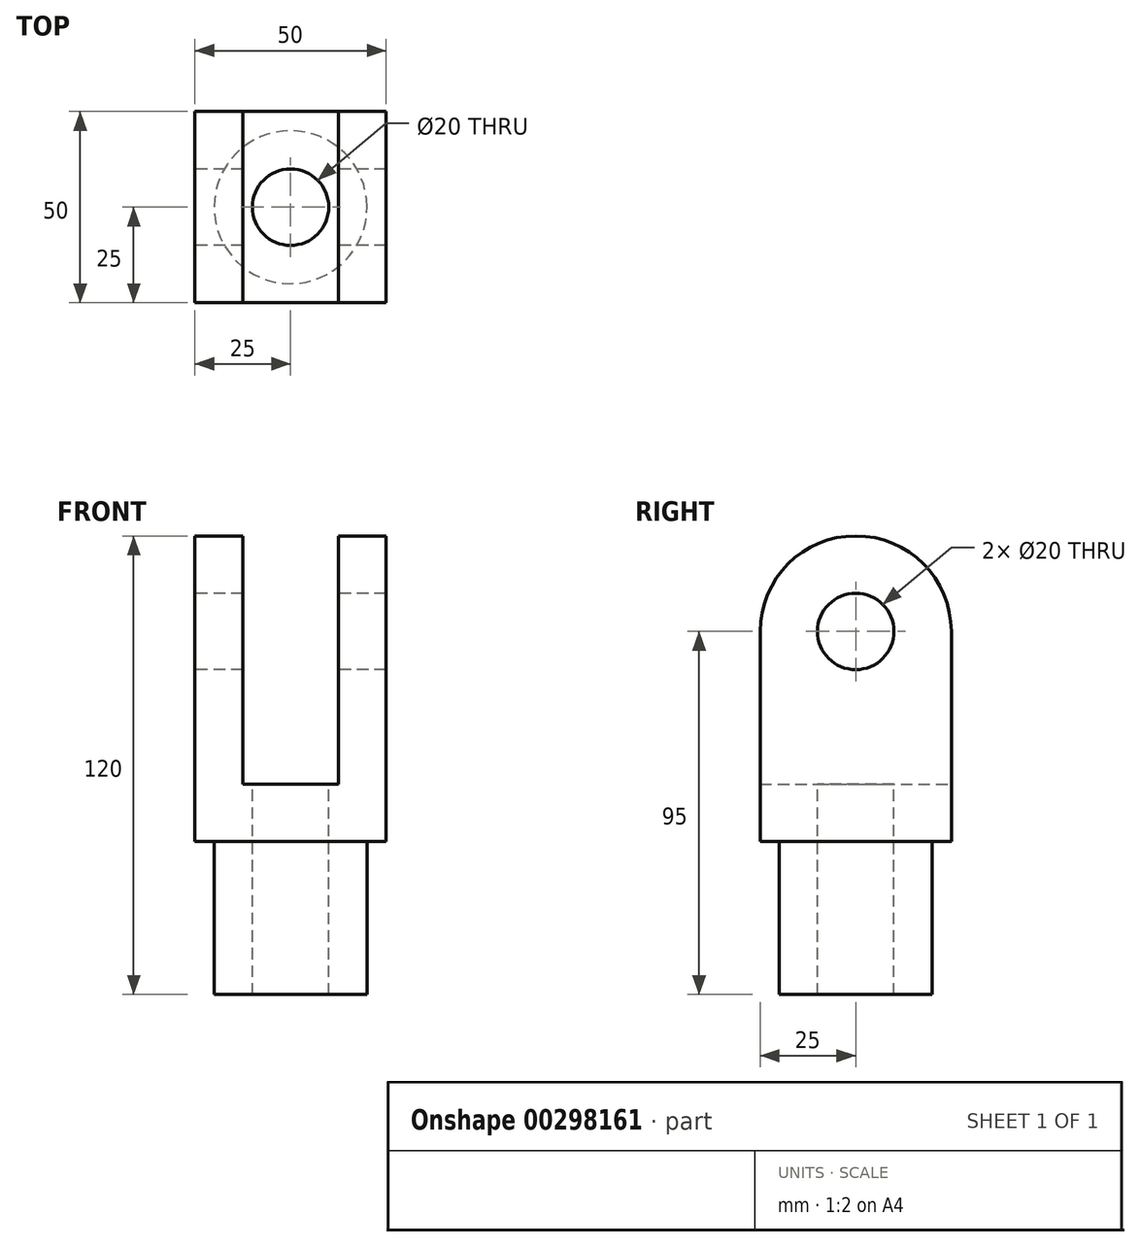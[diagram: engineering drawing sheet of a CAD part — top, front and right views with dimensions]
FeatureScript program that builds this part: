
annotation { "Feature Type Name" : "Feature", "Feature Type Description" : "" }
export const myFeature = defineFeature(function(context is Context, id is Id, definition is map)
    precondition{}
    {
        {
            var Q0;
            Q0=qCreatedBy(makeId("Front.planeOp"),FACE);
            var sketch = newSketch(context, id + "F0", { "sketchPlane" : qUnion([Q0])});
            skLineSegment(sketch, "E0.bottom", {"start": v(-25, 40) * mm, "end": v(25, 40) * mm});
            skLineSegment(sketch, "E0.top", {"start": v(-25, -40) * mm, "end": v(25, -40) * mm});
            skLineSegment(sketch, "E0.left", {"start": v(-25, 40) * mm, "end": v(-25, -40) * mm});
            skLineSegment(sketch, "E0.right", {"start": v(25, 40) * mm, "end": v(25, -40) * mm});
            skPoint(sketch, "E0.middle", {"position": v(0, 0) * mm});
            skLineSegment(sketch, "E1.bottom", {"start": v(12.5, 105) * mm, "end": v(-12.5, 105) * mm});
            skLineSegment(sketch, "E1.top", {"start": v(12.5, -25) * mm, "end": v(-12.5, -25) * mm});
            skLineSegment(sketch, "E1.left", {"start": v(12.5, 105) * mm, "end": v(12.5, -25) * mm});
            skLineSegment(sketch, "E1.right", {"start": v(-12.5, 105) * mm, "end": v(-12.5, -25) * mm});
            skPoint(sketch, "E1.middle", {"position": v(0, 40) * mm});
            skSolve(sketch);
        }
        {
            var Q0;
            Q0=makeQuery(id+"F0.imprint","IMPRINT",FACE,{"disambiguationData":[TD([[makeQuery(id+"F0.imprint","IMPRINT",EDGE,{"derivedFrom":sQuery(id+"F0.wireOp",EDGE,"E0.top")}),1.0]])]});
            extrude(context, id + "F1", {"entities" : qUnion([Q0]), "endBound" : BoundingType.SYMMETRIC, "depth" : 50 * mm});
        }
        {
            var Q0;
            Q0=makeQuery(id+"F1.opExtrude","SWEPT_FACE",FACE,{"disambiguationData":[OSD([sQuery(id+"F0.wireOp",EDGE,"E0.top")])]});
            var sketch = newSketch(context, id + "F2", { "sketchPlane" : qUnion([Q0])});
            skCircle(sketch, "E2", {"center": v(0, 0) * mm, "radius": 10 * mm});
            skCircle(sketch, "E3", {"center": v(0, 0) * mm, "radius": 20 * mm});
            skSolve(sketch);
        }
        {
            var Q0;
            Q0=makeQuery(id+"F2.imprint","IMPRINT",FACE,{"disambiguationData":[TD([[makeQuery(id+"F2.imprint","IMPRINT",EDGE,{"derivedFrom":sQuery(id+"F2.wireOp",EDGE,"E2")}),-1.0]])]});
            extrude(context, id + "F3", {"entities" : qUnion([Q0]), "operationType" : NewBodyOperationType.ADD, "depth" : 40 * mm});
        }
        {
            var Q0;
            Q0=makeQuery(id+"F2.imprint","IMPRINT",FACE,{"disambiguationData":[TD([[makeQuery(id+"F2.imprint","IMPRINT",EDGE,{"derivedFrom":sQuery(id+"F2.wireOp",EDGE,"E2")}),1.0]])]});
            extrude(context, id + "F4", {"entities" : qUnion([Q0]), "operationType" : NewBodyOperationType.REMOVE, "oppositeDirection" : true, "depth" : 15 * mm});
        }
        {
            var Q0;
            Q0=makeQuery(id+"F1.opExtrude","SWEPT_FACE",FACE,{"disambiguationData":[OSD([sQuery(id+"F0.wireOp",EDGE,"E0.left")])]});
            var sketch = newSketch(context, id + "F5", { "sketchPlane" : qUnion([Q0])});
            skLineSegment(sketch, "E4", {"start": v(-35.6, 15) * mm, "end": v(38.8, 15) * mm, "construction": true});
            skLineSegment(sketch, "E5", {"start": v(0, 48.87) * mm, "end": v(0, -47.95) * mm, "construction": true});
            skPoint(sketch, "E5.startSnap0", {"position": v(0, 40) * mm});
            skCircle(sketch, "E6", {"center": v(0, 15) * mm, "radius": 10 * mm});
            skSolve(sketch);
        }
        {
            var Q0;
            Q0=makeQuery(id+"F5.imprint","IMPRINT",FACE,{"disambiguationData":[TD([[makeQuery(id+"F5.imprint","IMPRINT",EDGE,{"derivedFrom":sQuery(id+"F5.wireOp",EDGE,"E6")}),1.0]])]});
            extrude(context, id + "F6", {"entities" : qUnion([Q0]), "operationType" : NewBodyOperationType.REMOVE, "oppositeDirection" : true, "depth" : 56.6 * mm});
        }
        {
            var Q0;
            {var subQ0=sQuery(id+"F0.wireOp",EDGE,"E0.bottom");Q0=makeQuery(id+"F1.opExtrude","CAP_EDGE",EDGE,{"disambiguationData":[OSD([subQ0]),TDD([makeQuery(id+"F0.imprint","IMPRINT",EDGE,{"disambiguationData":[TD([[makeQuery(id+"F0.imprint","INTERSECT",VERTEX,{"derivedFrom":[subQ0,sQuery(id+"F0.wireOp",EDGE,"E0.right")]}),1.0]])],"derivedFrom":subQ0})])],"isStart":true});}
            var Q1;
            {var subQ0=sQuery(id+"F0.wireOp",EDGE,"E0.bottom");Q1=makeQuery(id+"F1.opExtrude","CAP_EDGE",EDGE,{"disambiguationData":[OSD([subQ0]),TDD([makeQuery(id+"F0.imprint","IMPRINT",EDGE,{"disambiguationData":[TD([[makeQuery(id+"F0.imprint","INTERSECT",VERTEX,{"derivedFrom":[subQ0,sQuery(id+"F0.wireOp",EDGE,"E0.right")]}),1.0]])],"derivedFrom":subQ0})])],"isStart":false});}
            var Q2;
            {var subQ0=sQuery(id+"F0.wireOp",EDGE,"E0.bottom");Q2=makeQuery(id+"F1.opExtrude","CAP_EDGE",EDGE,{"disambiguationData":[OSD([subQ0]),TDD([makeQuery(id+"F0.imprint","IMPRINT",EDGE,{"disambiguationData":[TD([[makeQuery(id+"F0.imprint","INTERSECT",VERTEX,{"derivedFrom":[subQ0,sQuery(id+"F0.wireOp",EDGE,"E0.left")]}),-1.0]])],"derivedFrom":subQ0})])],"isStart":true});}
            var Q3;
            {var subQ0=sQuery(id+"F0.wireOp",EDGE,"E0.bottom");Q3=makeQuery(id+"F1.opExtrude","CAP_EDGE",EDGE,{"disambiguationData":[OSD([subQ0]),TDD([makeQuery(id+"F0.imprint","IMPRINT",EDGE,{"disambiguationData":[TD([[makeQuery(id+"F0.imprint","INTERSECT",VERTEX,{"derivedFrom":[subQ0,sQuery(id+"F0.wireOp",EDGE,"E0.left")]}),-1.0]])],"derivedFrom":subQ0})])],"isStart":false});}
            fillet(context, id + "F7", {"entities" : qUnion([Q0, Q1, Q2, Q3]), "radius" : 25 * mm, "tangentPropagation" : true, "allowEdgeOverflow" : false});
        }
    });
